# Revit family: MK
name_source: partatom
category: Mechanical Equipment
units: mm (PartAtom-declared; Revit-internal decimal feet)

## family parameters
Always vertical = Yes
Cut with Voids When Loaded = No
Part Type = Normal
Room Calculation Point = No
Round Connector Dimension = Use Diameter
Shared = No
Work Plane-Based = No

## types (4) — shared parameters
Case Fans (FLA) = Fans 120V
Case Fans (FLA)-2 = Fans 208V
Case Fans (FLA)-3 = Fans 460V
Description = 4-fan Evaporator
Elect. Defrost Amps-2 = Electric Def. Htrs. 460V
Elect. Defrost Amps-3 = Electric Def. Htrs. 120V
HEIGHT = 26.75 "
Manufacturer = Krack Corporation
Revit Family Dates = 08/26/2022SV
Type Comments = MK Series 2-Fan Evaporator
URL = www.krack.com
Voltage - 2 = 208 V
Voltage - 3 = 460 V
Voltage - Electrical Defrost - 2 = 460 V
WIDTH = 19 "

## per-type parameters (varying)
| type | 1-FAN | 2-FAN | 3-FAN | 4-FAN | Copper Pipes | L.SUPPORT | LENGTH | Phase - 2 | Phase - Elect. Def. - 2 | R.SUPPORT | SUPPORT HING |
| MK2 | No | Yes | No | No | Copper | 54 " | 65.38 " | 1 | 0 | 0 " | No |
| MK1 | Yes | No | No | No | <By Category> | 0 " | 38.38 " | 1 | 0 | 27 " | No |
| MK3 | No | No | Yes | No | Copper | 54 " | 92.38 " | 1 | 0 | 27 " | No |
| MK4 | No | No | No | Yes | Copper | 54 " | 119.38 " | 3 | 1 | 54 " | Yes |

note: column(s) folded — value = type name in every type: Model

## geometry (parser evidence)
native form markers: Sweep x19
no freeform markers — native parametric forms only
